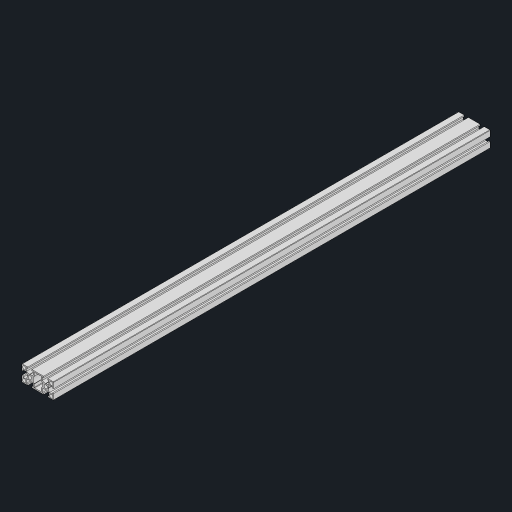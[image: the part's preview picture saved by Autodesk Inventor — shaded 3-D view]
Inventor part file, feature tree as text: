
AUTODESK INVENTOR PART (.ipt)
format: ipt  version: 2024.2 (Build 282272000, 272)  size: 320,512 bytes
history: native  units: mm
features: other x1, extrude x1, sketch x1
ambient origin geometry x8: Origin, YZ Plane, XZ Plane, XY Plane, X Axis, Y Axis, Z Axis, Center Point
bodies: Body1 (feature_tree)
feature tree (3):
  other  "솔리드1"
  extrude  "돌출1"  Depth=40.0mm
  sketch  "스케치1"
